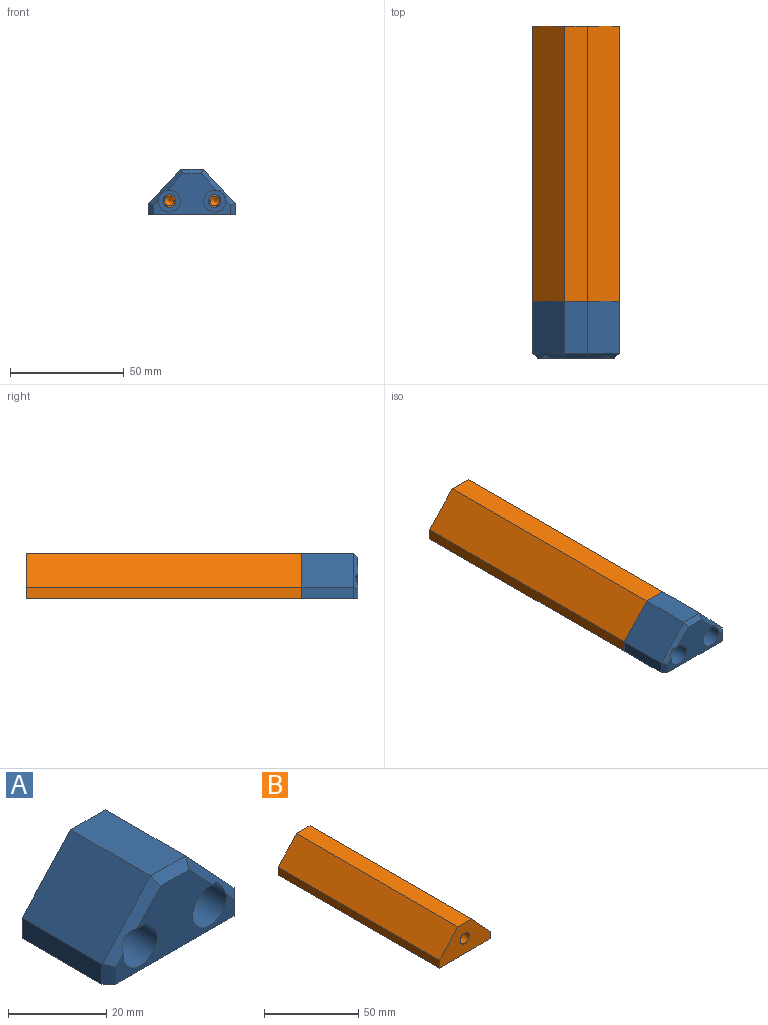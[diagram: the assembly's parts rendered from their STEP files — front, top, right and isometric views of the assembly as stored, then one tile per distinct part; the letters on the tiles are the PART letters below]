
ASSEMBLY  parts=2 mates=1
PART A: 19 faces, bbox 38x25x20 mm
  f0: plane 23x5mm, normal (-1,0,0), area 115mm2, adj f1,f5,f7,f18
  f1: plane 38x25mm, normal (0,0,-1), area 946mm2, adj f0,f2,f6,f7,f14,f18
  f2: plane 23x5mm, normal (1,0,0), area 115mm2, adj f1,f3,f7,f14
  f3: plane 23x15mm, normal (0.73,0,0.68), area 471.9mm2, adj f2,f4,f7,f15
  f4: plane 23x10mm, normal (0,0,1), area 230mm2, adj f3,f5,f7,f16
  f5: plane 23x15mm, normal (-0.73,0,0.68), area 471.9mm2, adj f0,f4,f7,f17
  f6: plane 34x18mm, normal (0,-1,0), area 293mm2, adj f1,f10,f13,f14,f15,f16,f17,f18
  f7: plane 38x20mm, normal (0,1,0), area 502.5mm2, adj f0,f1,f2,f3,f4,f5,f8,f11
  f8: cylinder r=2.75mm len=15mm, axis (0,-1,0), area 259.2mm2, adj f7,f9
  f9: plane 9.75x9.75mm, normal (0,-1,0), area 50.9mm2, adj f8,f10
  f10: cylinder r=4.88mm len=10mm, axis (0,-1,0), area 302.2mm2, adj f6,f9,f15
  f11: cylinder r=2.75mm len=15mm, axis (0,-1,0), area 259.2mm2, adj f7,f12
  f12: plane 9.75x9.75mm, normal (0,-1,0), area 50.9mm2, adj f11,f13
  f13: cylinder r=4.88mm len=10mm, axis (0,-1,0), area 302.2mm2, adj f6,f12,f17
  f14: plane 5x2mm, normal (0.71,-0.71,0), area 13mm2, adj f1,f2,f6,f15
  f15: plane 15.79x14.87mm, normal (0.52,-0.71,0.48), area 50.2mm2, adj f3,f6,f10,f14,f16
  f16: plane 10x2mm, normal (0,-0.71,0.71), area 25.8mm2, adj f4,f6,f15,f17
  f17: plane 15.79x14.87mm, normal (-0.52,-0.71,0.48), area 50.2mm2, adj f5,f6,f13,f16,f18
  f18: plane 5x2mm, normal (-0.71,-0.71,0), area 13mm2, adj f0,f1,f6,f17
PART B: 14 faces, bbox 38x121x20 mm
  f0: plane 121x5mm, normal (-1,0,0), area 605mm2, adj f1,f5,f6,f7
  f1: plane 121x38mm, normal (0,0,-1), area 4598mm2, adj f0,f2,f6,f7
  f2: plane 121x5mm, normal (1,0,0), area 605mm2, adj f1,f3,f6,f7
  f3: plane 121x15mm, normal (0.73,0,0.68), area 2482.7mm2, adj f2,f4,f6,f7
  f4: plane 121x10mm, normal (0,0,1), area 1210mm2, adj f3,f5,f6,f7
  f5: plane 121x15mm, normal (-0.73,0,0.68), area 2482.7mm2, adj f0,f4,f6,f7
  f6: plane 38x20mm, normal (0,-1,0), area 513.7mm2, adj f0,f1,f2,f3,f4,f5,f13
  f7: plane 38x20mm, normal (0,1,0), area 522.3mm2, adj f0,f1,f2,f3,f4,f5,f9,f11
  f8: cone r=0mm half-angle=59deg, axis (0,1,0), area 16.2mm2, adj f9
  f9: cylinder r=2.1mm len=20mm, axis (0,1,0), area 263.9mm2, adj f7,f8
  f10: cone r=0mm half-angle=59deg, axis (0,1,0), area 16.2mm2, adj f11
  f11: cylinder r=2.1mm len=20mm, axis (0,1,0), area 263.9mm2, adj f7,f10
  f12: cone r=0mm half-angle=59deg, axis (0,-1,0), area 42.4mm2, adj f13
  f13: cylinder r=3.4mm len=25mm, axis (0,-1,0), area 534.1mm2, adj f6,f12
PLACE A t=(-63.13,-13.44,-10.69)mm
PLACE B rot(axis=(0,0,1),180deg) t=(-25.13,-13.44,-10.69)mm
MATE fastened B.f10 <-> A.f8  axis (0,-1,0) through (-34.13,-13.44,-4.69)mm
